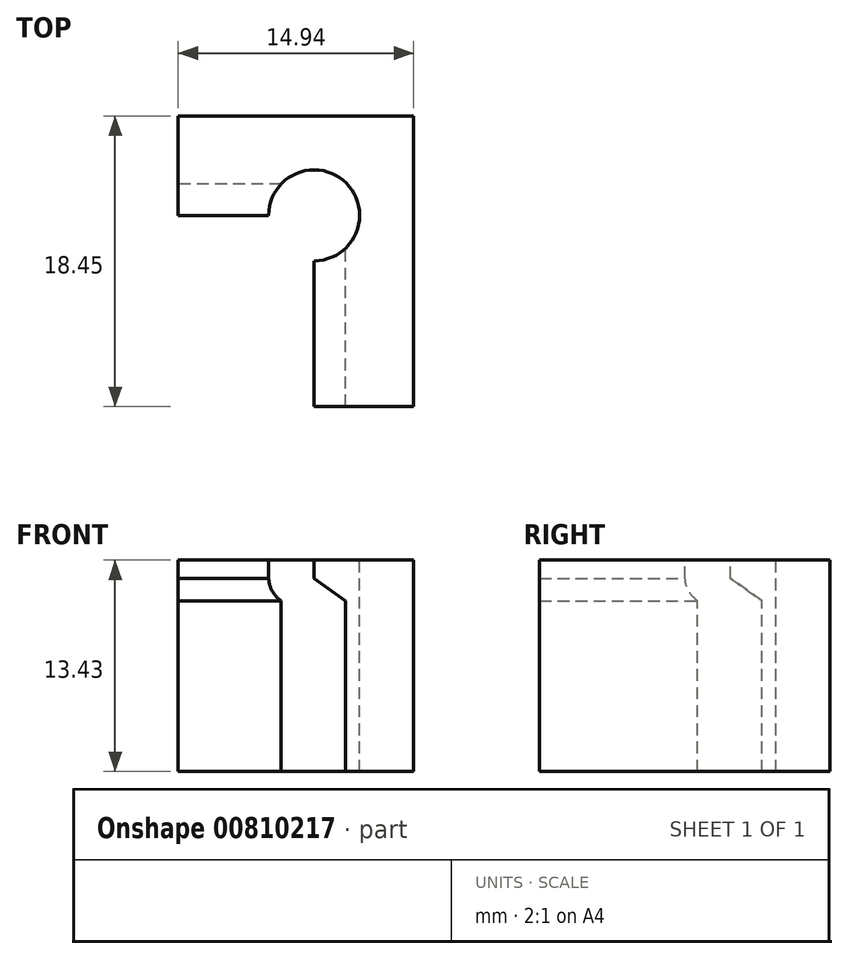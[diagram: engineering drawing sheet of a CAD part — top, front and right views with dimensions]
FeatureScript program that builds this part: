
annotation { "Feature Type Name" : "Feature", "Feature Type Description" : "" }
export const myFeature = defineFeature(function(context is Context, id is Id, definition is map)
    precondition{}
    {
        {
            var Q0;
            Q0=qCreatedBy(makeId("Front.planeOp"),FACE);
            var sketch = newSketch(context, id + "F0", { "sketchPlane" : qUnion([Q0])});
            skLineSegment(sketch, "E0", {"start": v(10.62, 0) * mm, "end": v(10.62, 10.83) * mm});
            skLineSegment(sketch, "E1", {"start": v(10.62, 10.83) * mm, "end": v(8.63, 12.27) * mm});
            skLineSegment(sketch, "E2", {"start": v(8.63, 12.27) * mm, "end": v(8.63, 13.43) * mm});
            skLineSegment(sketch, "E3", {"start": v(8.63, 13.43) * mm, "end": v(14.94, 13.43) * mm});
            skLineSegment(sketch, "E4", {"start": v(14.94, 13.43) * mm, "end": v(14.94, 0) * mm});
            skLineSegment(sketch, "E5", {"start": v(14.94, 0) * mm, "end": v(10.62, 0) * mm});
            skSolve(sketch);
        }
        {
            var Q0;
            Q0=qCreatedBy(makeId("Top.planeOp"),FACE);
            var sketch = newSketch(context, id + "F1", { "sketchPlane" : qUnion([Q0])});
            skLineSegment(sketch, "E6", {"start": v(10.62, 0) * mm, "end": v(10.62, 14.13) * mm});
            skLineSegment(sketch, "E7", {"start": v(10.62, 14.13) * mm, "end": v(0, 14.13) * mm});
            skSolve(sketch);
        }
        {
            var Q0;
            Q0=makeQuery(id+"F0.imprint","IMPRINT",FACE,{"disambiguationData":[TD([[makeQuery(id+"F0.imprint","IMPRINT",EDGE,{"derivedFrom":sQuery(id+"F0.wireOp",EDGE,"E0")}),-1.0]])]});
            var Q1;
            Q1=sQuery(id+"F1.wireOp",EDGE,"E6");
            var Q2;
            Q2=sQuery(id+"F1.wireOp",EDGE,"E7");
            sweep(context, id + "F2", {"profiles" : qUnion([Q0]), "path" : qUnion([Q1, Q2])});
        }
        {
            var Q0;
            Q0=makeQuery(id+"F2.opSweep","SWEPT_FACE",FACE,{"disambiguationData":[OSD([sQuery(id+"F0.wireOp",EDGE,"E3"),sQuery(id+"F1.wireOp",EDGE,"E6")])]});
            var sketch = newSketch(context, id + "F3", { "sketchPlane" : qUnion([Q0])});
            skCircle(sketch, "E8", {"center": v(8.63, 12.14) * mm, "radius": 2.89 * mm});
            skSolve(sketch);
        }
        {
            var Q0;
            Q0 = qSketchRegion(id + "F3", true);
            extrude(context, id + "F4", {"entities" : qUnion([Q0]), "operationType" : NewBodyOperationType.REMOVE, "oppositeDirection" : true, "depth" : 25 * mm, "offsetDistance" : 25 * mm});
        }
    });
